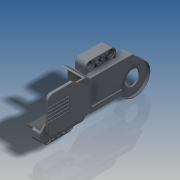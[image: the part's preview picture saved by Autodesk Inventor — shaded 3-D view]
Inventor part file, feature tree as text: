
AUTODESK INVENTOR PART (.ipt)
format: ipt  version: 2016 SP2 (Build 200236200, 236)  size: 919,552 bytes
history: native  units: in
note: dims shown in document units (in); Inventor stores cm internally (conversion verified against a paired STEP export)
features: extrude x19, sketch x7, plane x2, fillet x1
ambient origin geometry x8: Origin, YZ Plane, XZ Plane, XY Plane, X Axis, Y Axis, Z Axis, Center Point
bodies: Solid1 (feature_tree)
feature tree (29):
  sketch  "Sketch2"  dims[d0=0.9134in d1=0.8819in]
  extrude  "Extrusion1"  Depth=0.8819in
  extrude  "Extrusion2"  Depth=0.1417in
  extrude  "Extrusion3"  Depth=0.7717in
  sketch  "Sketch3"  dims[d2=0.4409in d4=0.1417in]
  extrude  "Extrusion7"  Depth=0.2992in
  extrude  "Extrusion4"  Depth=1.0866in
  extrude  "Extrusion5"  Depth=0.1575in
  extrude  "Extrusion6"  Depth=0.315in
  extrude  "Extrusion8"  Depth=0.0157in
  extrude  "Extrusion9"  Depth=0.0157in
  extrude  "Extrusion10"  Depth=0.2992in
  extrude  "Extrusion11"  Depth=0.1417in
  extrude  "Extrusion12"  Depth=0.0157in
  plane  "Work Plane1"
  sketch  "Sketch6"  dims[d9=1.4331in d10=1.0866in]
  extrude  "Extrusion13"  Depth=0.0472in
  extrude  "Extrusion14"  Depth=0.0157in
  extrude  "Extrusion15"  Depth=0.0472in
  plane  "Work Plane2"
  sketch  "Sketch7"  dims[d11=1.748in d12=0.1575in]
  extrude  "Extrusion16"  Depth=0.0945in
  extrude  "Extrusion17"  Depth=0.0472in
  extrude  "Extrusion18"  Depth=0.0157in
  extrude  "Extrusion19"  Depth=0.0472in
  fillet  "Fillet1"  Radius=0.063in
  sketch  "Sketch4"  dims[d5=0.1417in d6=0.7717in]
  sketch  "Sketch5"  dims[d7=45.0deg d8=0.2992in]
  sketch  "Sketch8"  dims[d13=0.2835in d14=0.315in d15=1.3543in d16=1.5591in d17=0.2992in d18=0.1417in d19=0.8119in d20=0.0472in d21=0.0557in d22=0.0472in d23=0.0945in d24=0.0472in d25=0.0413in d26=0.0472in d27=0.063in d28=0.0445in d29=0.0887in d32=0.0106in d33=0.2992in d34=0.0in d35=0.5039in d36=0.1417in d37=0.0in d38=0.2205in d39=0.0in d40=0.2835in d41=0.5669in d42=0.1102in d43=0.0157in d44=0.315in d45=0.3937in d46=0.0in d47=0.1575in d48=0.0in d49=0.1575in d50=0.1417in d51=0.1575in d52=1.2441in d53=1.0866in d54=0.5039in d55=0.378in d56=0.2047in d57=0.0787in d58=0.0in d59=0.1732in d60=0.1448in d61=0.0315in d62=-0.1855in d63=0.0315in d64=0.0in d65=0.6299in d66=0.0472in d74=0.2677in d75=1.9685in d77=0.0945in d78=0.3937in d80=0.3937in d82=0.0157in d83=0.0in d84=0.2677in d85=0.6457in d86=0.0in d87=0.2992in d88=0.315in d89=0.4094in d90=0.0in d91=0.252in d92=0.0in d93=0.0945in d94=0.0in d95=-0.0157in d96=0.315in d97=0.1732in d98=0.2835in d99=45.0deg d100=0.3307in d101=0.0472in d102=0.2441in d103=0.189in d104=0.063in d105=0.063in d106=0.0in d107=0.252in d108=0.0in d109=0.315in d110=0.0in d111=-0.2992in d112=0.315in d113=0.3307in d114=0.0472in d115=0.2441in d116=0.189in d117=0.063in d118=0.063in d119=0.0in d120=0.252in d121=0.0in d122=0.315in d123=0.0in d124=0.252in d125=0.315in d126=0.0in d127=0.0039in d128=0.0157in]
